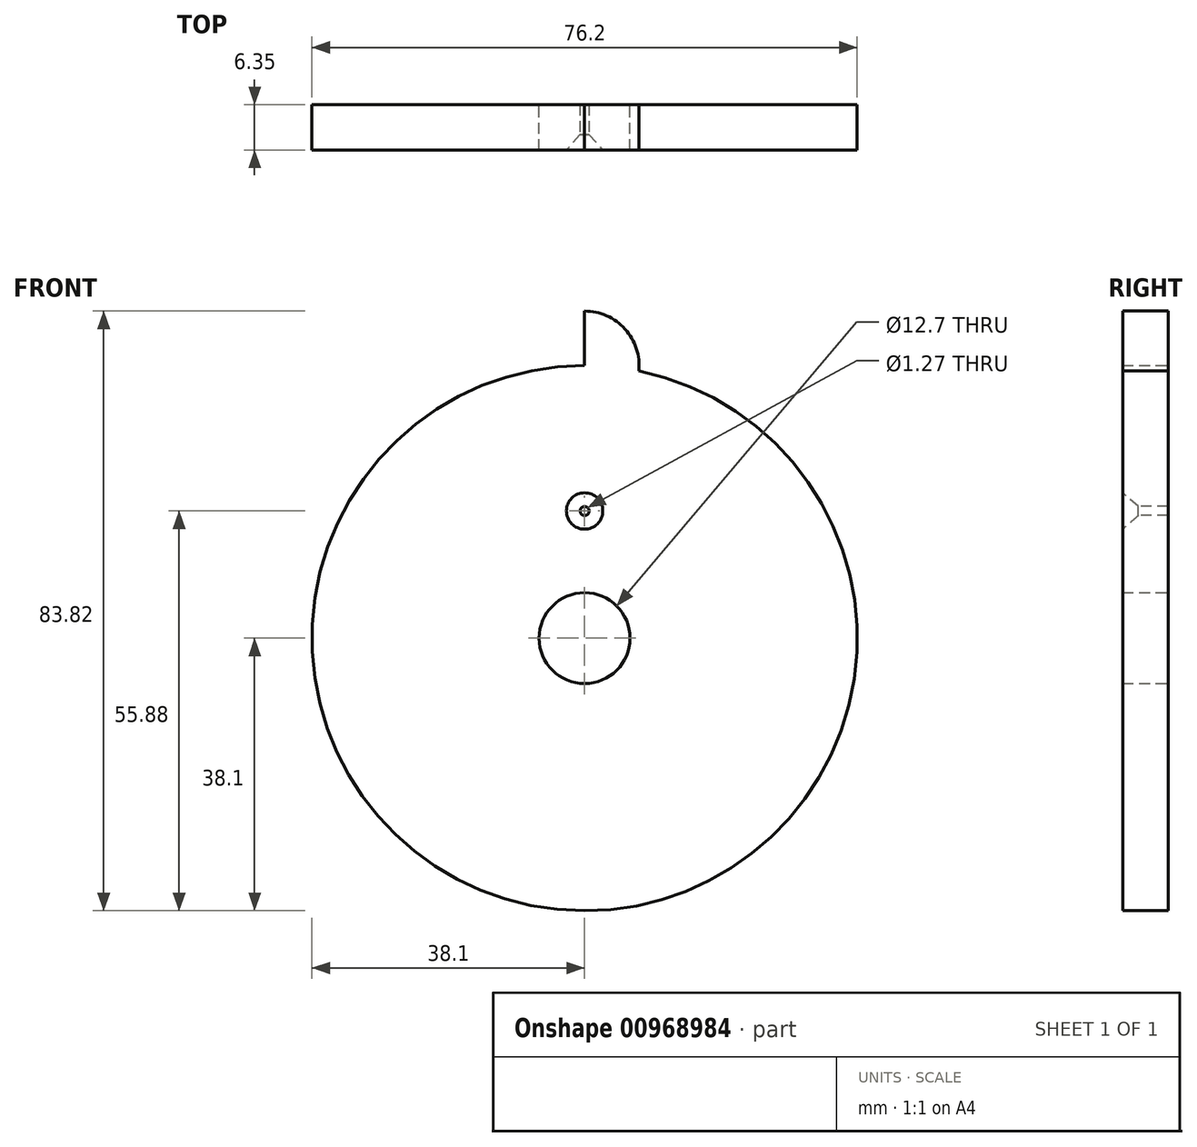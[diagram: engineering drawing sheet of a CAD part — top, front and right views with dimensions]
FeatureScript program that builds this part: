
annotation { "Feature Type Name" : "Feature", "Feature Type Description" : "" }
export const myFeature = defineFeature(function(context is Context, id is Id, definition is map)
    precondition{}
    {
        {
            var Q0;
            Q0=qCreatedBy(makeId("Front.planeOp"),FACE);
            var sketch = newSketch(context, id + "F0", { "sketchPlane" : qUnion([Q0])});
            skCircle(sketch, "E0", {"center": v(0, 0) * mm, "radius": 38.1 * mm});
            skLineSegment(sketch, "E1", {"start": v(0, 38.1) * mm, "end": v(0, 45.72) * mm});
            skArc(sketch, "E2", {"start": v(0, 45.72) * mm, "mid": v(5.65, 43.21) * mm, "end": v(7.58, 37.34) * mm});
            skArc(sketch, "E3.1.0", {"start": v(-32.33, 32.33) * mm, "mid": v(-26.56, 34.55) * mm, "end": v(-21.04, 31.76) * mm});
            skLineSegment(sketch, "E3.1.1", {"start": v(-26.94, 26.94) * mm, "end": v(-32.33, 32.33) * mm});
            skArc(sketch, "E3.2.0", {"start": v(-45.72, 0) * mm, "mid": v(-43.21, 5.65) * mm, "end": v(-37.34, 7.58) * mm});
            skLineSegment(sketch, "E3.2.1", {"start": v(-38.1, 0) * mm, "end": v(-45.72, 0) * mm});
            skArc(sketch, "E4.1.3.0", {"start": v(-32.33, -32.33) * mm, "mid": v(-34.55, -26.56) * mm, "end": v(-31.76, -21.04) * mm});
            skLineSegment(sketch, "E4.4.3.0", {"start": v(-26.94, -26.94) * mm, "end": v(-32.33, -32.33) * mm});
            skArc(sketch, "E4.1.4.0", {"start": v(0, -45.72) * mm, "mid": v(-5.65, -43.21) * mm, "end": v(-7.58, -37.34) * mm});
            skLineSegment(sketch, "E4.4.4.0", {"start": v(0, -38.1) * mm, "end": v(0, -45.72) * mm});
            skArc(sketch, "E4.1.5.0", {"start": v(32.33, -32.33) * mm, "mid": v(26.56, -34.55) * mm, "end": v(21.04, -31.76) * mm});
            skLineSegment(sketch, "E4.4.5.0", {"start": v(26.94, -26.94) * mm, "end": v(32.33, -32.33) * mm});
            skArc(sketch, "E4.1.6.0", {"start": v(45.72, 0) * mm, "mid": v(43.21, -5.65) * mm, "end": v(37.34, -7.58) * mm});
            skLineSegment(sketch, "E4.4.6.0", {"start": v(38.1, 0) * mm, "end": v(45.72, 0) * mm});
            skArc(sketch, "E4.1.7.0", {"start": v(32.33, 32.33) * mm, "mid": v(34.55, 26.56) * mm, "end": v(31.76, 21.04) * mm});
            skLineSegment(sketch, "E4.4.7.0", {"start": v(26.94, 26.94) * mm, "end": v(32.33, 32.33) * mm});
            skCircle(sketch, "E5", {"center": v(0, 0) * mm, "radius": 6.35 * mm});
            skSolve(sketch);
        }
        {
            var Q0;
            {var subQ0=sQuery(id+"F0.wireOp",EDGE,"E0");var subQ8=makeQuery(id+"F0.imprint","INTERSECT",VERTEX,{"derivedFrom":[subQ0,sQuery(id+"F0.wireOp",EDGE,"E4.4.6.0")]});Q0=makeQuery(id+"F0.imprint","IMPRINT",FACE,{"disambiguationData":[TD([[makeQuery(id+"F0.imprint","IMPRINT",EDGE,{"disambiguationData":[TD([[subQ8,-1.0]])],"derivedFrom":subQ0}),1.0]])]});}
            var Q1;
            {var subQ0=sQuery(id+"F0.wireOp",EDGE,"E3.1.0");Q1=makeQuery(id+"F0.imprint","IMPRINT",FACE,{"disambiguationData":[TD([[makeQuery(id+"F0.imprint","IMPRINT",EDGE,{"derivedFrom":subQ0}),-1.0]])]});}
            var Q2;
            {var subQ0=sQuery(id+"F0.wireOp",EDGE,"E1");Q2=makeQuery(id+"F0.imprint","IMPRINT",FACE,{"disambiguationData":[TD([[makeQuery(id+"F0.imprint","IMPRINT",EDGE,{"derivedFrom":subQ0}),-1.0]])]});}
            var Q3;
            {var subQ0=sQuery(id+"F0.wireOp",EDGE,"E4.1.7.0");Q3=makeQuery(id+"F0.imprint","IMPRINT",FACE,{"disambiguationData":[TD([[makeQuery(id+"F0.imprint","IMPRINT",EDGE,{"derivedFrom":subQ0}),-1.0]])]});}
            var Q4;
            {var subQ0=sQuery(id+"F0.wireOp",EDGE,"E4.1.6.0");Q4=makeQuery(id+"F0.imprint","IMPRINT",FACE,{"disambiguationData":[TD([[makeQuery(id+"F0.imprint","IMPRINT",EDGE,{"derivedFrom":subQ0}),-1.0]])]});}
            var Q5;
            {var subQ0=sQuery(id+"F0.wireOp",EDGE,"E4.1.5.0");Q5=makeQuery(id+"F0.imprint","IMPRINT",FACE,{"disambiguationData":[TD([[makeQuery(id+"F0.imprint","IMPRINT",EDGE,{"derivedFrom":subQ0}),-1.0]])]});}
            var Q6;
            {var subQ0=sQuery(id+"F0.wireOp",EDGE,"E4.1.4.0");Q6=makeQuery(id+"F0.imprint","IMPRINT",FACE,{"disambiguationData":[TD([[makeQuery(id+"F0.imprint","IMPRINT",EDGE,{"derivedFrom":subQ0}),-1.0]])]});}
            var Q7;
            {var subQ0=sQuery(id+"F0.wireOp",EDGE,"E4.1.3.0");Q7=makeQuery(id+"F0.imprint","IMPRINT",FACE,{"disambiguationData":[TD([[makeQuery(id+"F0.imprint","IMPRINT",EDGE,{"derivedFrom":subQ0}),-1.0]])]});}
            var Q8;
            {var subQ0=sQuery(id+"F0.wireOp",EDGE,"E3.2.0");Q8=makeQuery(id+"F0.imprint","IMPRINT",FACE,{"disambiguationData":[TD([[makeQuery(id+"F0.imprint","IMPRINT",EDGE,{"derivedFrom":subQ0}),-1.0]])]});}
            extrude(context, id + "F1", {"entities" : qUnion([Q0, Q1, Q2, Q3, Q4, Q5, Q6, Q7, Q8]), "depth" : 6.35 * mm, "offsetDistance" : 25.4 * mm});
        }
        {
            var Q0;
            Q0=makeQuery(id+"F1.opExtrude","CAP_FACE",FACE,{"disambiguationData":[OSD([sQuery(id+"F0.wireOp",EDGE,"E0"),sQuery(id+"F0.wireOp",EDGE,"E1"),sQuery(id+"F0.wireOp",EDGE,"E2"),sQuery(id+"F0.wireOp",EDGE,"E3.1.0"),sQuery(id+"F0.wireOp",EDGE,"E3.1.1"),sQuery(id+"F0.wireOp",EDGE,"E3.2.0"),sQuery(id+"F0.wireOp",EDGE,"E3.2.1"),sQuery(id+"F0.wireOp",EDGE,"E4.1.3.0"),sQuery(id+"F0.wireOp",EDGE,"E4.4.3.0"),sQuery(id+"F0.wireOp",EDGE,"E4.1.4.0"),sQuery(id+"F0.wireOp",EDGE,"E4.4.4.0"),sQuery(id+"F0.wireOp",EDGE,"E4.1.5.0"),sQuery(id+"F0.wireOp",EDGE,"E4.4.5.0"),sQuery(id+"F0.wireOp",EDGE,"E4.1.6.0"),sQuery(id+"F0.wireOp",EDGE,"E4.4.6.0"),sQuery(id+"F0.wireOp",EDGE,"E4.1.7.0"),sQuery(id+"F0.wireOp",EDGE,"E4.4.7.0"),sQuery(id+"F0.wireOp",EDGE,"E5")])],"isStart":false});
            var sketch = newSketch(context, id + "F2", { "sketchPlane" : qUnion([Q0])});
            skPoint(sketch, "E6", {"position": v(0, 17.78) * mm});
            skSolve(sketch);
        }
        {
            var Q0;
            Q0=sQuery(id+"F2.wireOp",VERTEX,"E6");
            var Q1;
            Q1=makeQuery(id+"F1.opExtrude","SWEPT_BODY",BODY,{"disambiguationData":[OSD([sQuery(id+"F0.wireOp",EDGE,"E0"),sQuery(id+"F0.wireOp",EDGE,"E1"),sQuery(id+"F0.wireOp",EDGE,"E2"),sQuery(id+"F0.wireOp",EDGE,"E3.1.0"),sQuery(id+"F0.wireOp",EDGE,"E3.1.1"),sQuery(id+"F0.wireOp",EDGE,"E3.2.0"),sQuery(id+"F0.wireOp",EDGE,"E3.2.1"),sQuery(id+"F0.wireOp",EDGE,"E4.1.3.0"),sQuery(id+"F0.wireOp",EDGE,"E4.4.3.0"),sQuery(id+"F0.wireOp",EDGE,"E4.1.4.0"),sQuery(id+"F0.wireOp",EDGE,"E4.4.4.0"),sQuery(id+"F0.wireOp",EDGE,"E4.1.5.0"),sQuery(id+"F0.wireOp",EDGE,"E4.4.5.0"),sQuery(id+"F0.wireOp",EDGE,"E4.1.6.0"),sQuery(id+"F0.wireOp",EDGE,"E4.4.6.0"),sQuery(id+"F0.wireOp",EDGE,"E4.1.7.0"),sQuery(id+"F0.wireOp",EDGE,"E4.4.7.0"),sQuery(id+"F0.wireOp",EDGE,"E5")])]});
            hole(context, id + "F3", {"style" : HoleStyle.C_SINK, "endStyle" : HoleEndStyle.BLIND, "holeDiameter" : 1.27 * mm, "cSinkDiameter" : 5.08 * mm, "cSinkAngle" : 82 * degree, "majorDiameter" : 6.35 * mm, "holeDepth" : 6.35 * mm, "isTappedThrough" : true, "tappedDepth" : 12.7 * mm, "tapClearance" : 3, "locations" : qUnion([Q0]), "scope" : qUnion([Q1])});
        }
    });
